# Revit family: 01 Isku Amphi
name_source: partatom
category: Furniture
revit_build: Autodesk Revit 2015 (Build: 20140606_1530(x64)
units: mm (PartAtom-declared; Revit-internal decimal feet)

## types (6) — shared parameters
Available as antimicrobial = Yes
Depth = 500 mm  [stored 1.64042 ft]
Manufacturer = Isku Oy
Model = 3754
URL = www.isku.fi
Width = 1053 mm  [stored 3.45472 ft]
zero-valued in all types: NominalDepth, NominalHeight, NominalLength

## per-type parameters (varying)
| type | Amphi A | Amphi B | Amphi mod. | Height |
| 3754 AMPHI A 26 cm | Yes | No | Isku Amphi A : 3754 AMPHI A 26 cm | 260 mm  [stored 0.853018 ft] |
| 3754 AMPHI A 40 cm | Yes | No | Isku Amphi A : 3754 AMPHI A 40 cm | 400 mm  [stored 1.31234 ft] |
| 3754 AMPHI A 54 cm | Yes | No | Isku Amphi A : 3754 AMPHI A 54 cm | 540 mm  [stored 1.77165 ft] |
| 3754 AMPHI B 26 cm | No | Yes | Isku Amphi A : 3754 AMPHI A 26 cm | 260 mm  [stored 0.853018 ft] |
| 3754 AMPHI B 40 cm | No | Yes | Isku Amphi A : 3754 AMPHI A 40 cm | 400 mm  [stored 1.31234 ft] |
| 3754 AMPHI B 54 cm | No | Yes | Isku Amphi A : 3754 AMPHI A 54 cm | 540 mm  [stored 1.77165 ft] |

note: [stored X ft] marks values corroborated as IEEE doubles in the binary element streams (Revit-internal decimal feet)

## geometry (parser evidence)
native form markers: Sweep x5
no freeform markers — native parametric forms only
